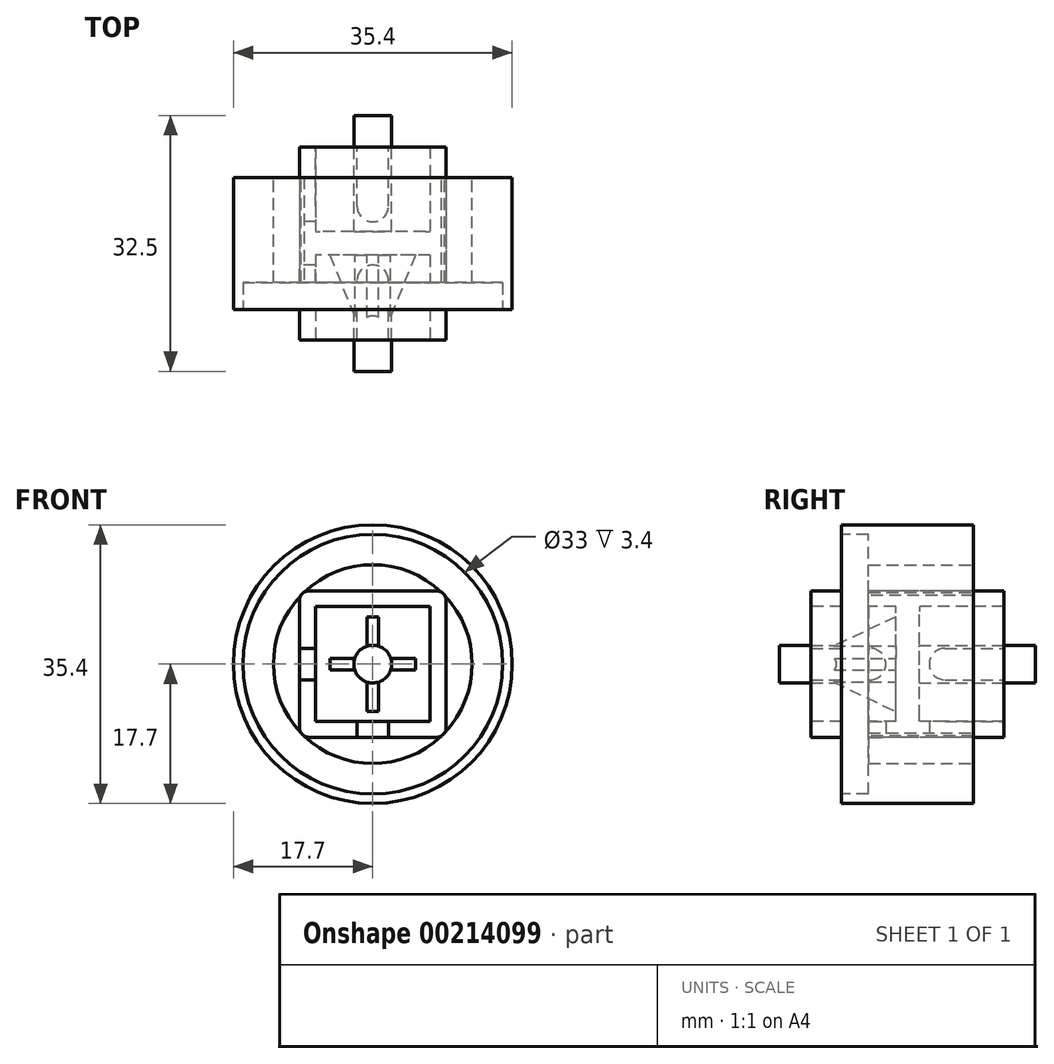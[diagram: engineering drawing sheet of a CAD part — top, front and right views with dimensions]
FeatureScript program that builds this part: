
annotation { "Feature Type Name" : "Feature", "Feature Type Description" : "" }
export const myFeature = defineFeature(function(context is Context, id is Id, definition is map)
    precondition{}
    {
        {
            var Q0;
            Q0=qCreatedBy(makeId("Front.planeOp"),FACE);
            var sketch = newSketch(context, id + "F0", { "sketchPlane" : qUnion([Q0])});
            skCircle(sketch, "E0", {"center": v(0, 0) * mm, "radius": 12.62 * mm});
            skCircle(sketch, "E1", {"center": v(0, 0) * mm, "radius": 17.7 * mm});
            skSolve(sketch);
        }
        {
            var Q0;
            Q0 = qSketchRegion(id + "F0", true);
            extrude(context, id + "F1", {"entities" : qUnion([Q0]), "endBound" : BoundingType.SYMMETRIC, "depth" : 16.75 * mm});
        }
        {
            var Q0;
            Q0=qCreatedBy(makeId("Front.planeOp"),FACE);
            var sketch = newSketch(context, id + "F2", { "sketchPlane" : qUnion([Q0])});
            skLineSegment(sketch, "E2.bottom", {"start": v(-9.3, 9.3) * mm, "end": v(9.3, 9.3) * mm});
            skLineSegment(sketch, "E2.top", {"start": v(-9.3, -9.3) * mm, "end": v(9.3, -9.3) * mm});
            skLineSegment(sketch, "E2.left", {"start": v(-9.3, 9.3) * mm, "end": v(-9.3, -9.3) * mm});
            skLineSegment(sketch, "E2.right", {"start": v(9.3, 9.3) * mm, "end": v(9.3, -9.3) * mm});
            skLineSegment(sketch, "E3", {"start": v(0, 41.14) * mm, "end": v(0, -47.29) * mm, "construction": true});
            skLineSegment(sketch, "E4", {"start": v(-35, 0) * mm, "end": v(39.07, 0) * mm, "construction": true});
            skSolve(sketch);
        }
        {
            var Q0;
            Q0=makeQuery(id+"F2.imprint","IMPRINT",FACE,{"disambiguationData":[TD([[makeQuery(id+"F2.imprint","IMPRINT",EDGE,{"derivedFrom":sQuery(id+"F2.wireOp",EDGE,"E2.bottom")}),-1.0]])]});
            extrude(context, id + "F3", {"entities" : qUnion([Q0]), "endBound" : BoundingType.SYMMETRIC, "oppositeDirection" : true, "depth" : 24.5 * mm});
        }
        {
            var Q0;
            Q0=makeQuery(id+"F3.opExtrude","CAP_FACE",FACE,{"disambiguationData":[OSD([sQuery(id+"F2.wireOp",EDGE,"E2.bottom"),sQuery(id+"F2.wireOp",EDGE,"E2.top"),sQuery(id+"F2.wireOp",EDGE,"E2.left"),sQuery(id+"F2.wireOp",EDGE,"E2.right")])],"isStart":true});
            var sketch = newSketch(context, id + "F4", { "sketchPlane" : qUnion([Q0])});
            skLineSegment(sketch, "E5.bottom", {"start": v(-7.3, 7.3) * mm, "end": v(7.3, 7.3) * mm});
            skLineSegment(sketch, "E5.top", {"start": v(-7.3, -7.3) * mm, "end": v(7.3, -7.3) * mm});
            skLineSegment(sketch, "E5.left", {"start": v(-7.3, 7.3) * mm, "end": v(-7.3, -7.3) * mm});
            skLineSegment(sketch, "E5.right", {"start": v(7.3, 7.3) * mm, "end": v(7.3, -7.3) * mm});
            skSolve(sketch);
        }
        {
            var Q0;
            Q0=makeQuery(id+"F1.opExtrude","CAP_FACE",FACE,{"disambiguationData":[OSD([sQuery(id+"F0.wireOp",EDGE,"E0"),sQuery(id+"F0.wireOp",EDGE,"E1")])],"isStart":false});
            var sketch = newSketch(context, id + "F5", { "sketchPlane" : qUnion([Q0])});
            skCircle(sketch, "E6", {"center": v(0, 0) * mm, "radius": 16.5 * mm});
            skSolve(sketch);
        }
        {
            var Q0;
            Q0 = qSketchRegion(id + "F5", true);
            extrude(context, id + "F6", {"entities" : qUnion([Q0]), "operationType" : NewBodyOperationType.REMOVE, "oppositeDirection" : true, "depth" : 3.4 * mm});
        }
        {
            var Q0;
            Q0=makeQuery(id+"F3.opExtrude","SWEPT_EDGE",EDGE,{"disambiguationData":[OSD([sQuery(id+"F2.wireOp",EDGE,"E2.bottom"),sQuery(id+"F2.wireOp",EDGE,"E2.left")])]});
            var Q1;
            Q1=makeQuery(id+"F3.opExtrude","SWEPT_EDGE",EDGE,{"disambiguationData":[OSD([sQuery(id+"F2.wireOp",EDGE,"E2.top"),sQuery(id+"F2.wireOp",EDGE,"E2.left")])]});
            var Q2;
            Q2=makeQuery(id+"F3.opExtrude","SWEPT_EDGE",EDGE,{"disambiguationData":[OSD([sQuery(id+"F2.wireOp",EDGE,"E2.top"),sQuery(id+"F2.wireOp",EDGE,"E2.right")])]});
            var Q3;
            Q3=makeQuery(id+"F3.opExtrude","SWEPT_EDGE",EDGE,{"disambiguationData":[OSD([sQuery(id+"F2.wireOp",EDGE,"E2.bottom"),sQuery(id+"F2.wireOp",EDGE,"E2.right")])]});
            fillet(context, id + "F7", {"entities" : qUnion([Q0, Q1, Q2, Q3]), "radius" : 1.2 * mm, "tangentPropagation" : true, "allowEdgeOverflow" : false});
        }
        {
            var Q0;
            Q0 = qSketchRegion(id + "F4", true);
            extrude(context, id + "F8", {"entities" : qUnion([Q0]), "operationType" : NewBodyOperationType.REMOVE, "endBound" : BoundingType.THROUGH_ALL, "oppositeDirection" : true, "depth" : 10 * mm});
        }
        {
            var Q0;
            Q0=qCreatedBy(makeId("Front.planeOp"),FACE);
            var sketch = newSketch(context, id + "F9", { "sketchPlane" : qUnion([Q0])});
            skLineSegment(sketch, "E7.0", {"start": v(-9.3, 8.1) * mm, "end": v(-9.3, -8.1) * mm});
            skLineSegment(sketch, "E7.1", {"start": v(-8.1, 9.3) * mm, "end": v(8.1, 9.3) * mm});
            skArc(sketch, "E7.2", {"start": v(-8.1, 9.3) * mm, "mid": v(-8.95, 8.95) * mm, "end": v(-9.3, 8.1) * mm});
            skArc(sketch, "E7.3", {"start": v(9.3, 8.1) * mm, "mid": v(8.95, 8.95) * mm, "end": v(8.1, 9.3) * mm});
            skLineSegment(sketch, "E7.4", {"start": v(9.3, 8.1) * mm, "end": v(9.3, -8.1) * mm});
            skArc(sketch, "E7.5", {"start": v(-9.3, -8.1) * mm, "mid": v(-8.95, -8.95) * mm, "end": v(-8.1, -9.3) * mm});
            skLineSegment(sketch, "E7.6", {"start": v(-8.1, -9.3) * mm, "end": v(8.1, -9.3) * mm});
            skArc(sketch, "E7.7", {"start": v(8.1, -9.3) * mm, "mid": v(8.95, -8.95) * mm, "end": v(9.3, -8.1) * mm});
            skSolve(sketch);
        }
        {
            var Q0;
            Q0 = qSketchRegion(id + "F9", true);
            extrude(context, id + "F10", {"entities" : qUnion([Q0]), "operationType" : NewBodyOperationType.ADD, "endBound" : BoundingType.SYMMETRIC, "depth" : 3 * mm});
        }
        {
            var Q0;
            Q0=qCreatedBy(makeId("Front.planeOp"),FACE);
            var sketch = newSketch(context, id + "F11", { "sketchPlane" : qUnion([Q0])});
            skCircle(sketch, "E8", {"center": v(0, 0) * mm, "radius": 2.4 * mm});
            skSolve(sketch);
        }
        {
            var Q0;
            Q0 = qSketchRegion(id + "F11", true);
            extrude(context, id + "F12", {"entities" : qUnion([Q0]), "operationType" : NewBodyOperationType.ADD, "endBound" : BoundingType.SYMMETRIC, "depth" : 32.5 * mm});
        }
        {
            var Q0;
            {var subQ0=sQuery(id+"F4.wireOp",EDGE,"E5.top");var subQ1=sQuery(id+"F4.wireOp",EDGE,"E5.left");Q0=makeQuery(id+"F10.boolean.opBoolean","SPLIT",EDGE,{"disambiguationData":[TD([makeQuery(id+"F3.opExtrude","CAP_FACE",FACE,{"disambiguationData":[OSD([sQuery(id+"F2.wireOp",EDGE,"E2.bottom"),sQuery(id+"F2.wireOp",EDGE,"E2.top"),sQuery(id+"F2.wireOp",EDGE,"E2.left"),sQuery(id+"F2.wireOp",EDGE,"E2.right")])],"isStart":false})])],"derivedFrom":makeQuery(id+"F8.boolean.opBoolean","COPY",EDGE,{"derivedFrom":makeQuery(id+"F8.opExtrude","SWEPT_EDGE",EDGE,{"disambiguationData":[OSD([subQ0,subQ1])]})})});}
            var Q1;
            {var subQ0=sQuery(id+"F4.wireOp",EDGE,"E5.bottom");var subQ1=sQuery(id+"F4.wireOp",EDGE,"E5.left");Q1=makeQuery(id+"F10.boolean.opBoolean","SPLIT",EDGE,{"disambiguationData":[TD([makeQuery(id+"F3.opExtrude","CAP_FACE",FACE,{"disambiguationData":[OSD([sQuery(id+"F2.wireOp",EDGE,"E2.bottom"),sQuery(id+"F2.wireOp",EDGE,"E2.top"),sQuery(id+"F2.wireOp",EDGE,"E2.left"),sQuery(id+"F2.wireOp",EDGE,"E2.right")])],"isStart":false})])],"derivedFrom":makeQuery(id+"F8.boolean.opBoolean","COPY",EDGE,{"derivedFrom":makeQuery(id+"F8.opExtrude","SWEPT_EDGE",EDGE,{"disambiguationData":[OSD([subQ0,subQ1])]})})});}
            var Q2;
            {var subQ0=sQuery(id+"F4.wireOp",EDGE,"E5.bottom");var subQ1=sQuery(id+"F4.wireOp",EDGE,"E5.right");Q2=makeQuery(id+"F10.boolean.opBoolean","SPLIT",EDGE,{"disambiguationData":[TD([makeQuery(id+"F3.opExtrude","CAP_FACE",FACE,{"disambiguationData":[OSD([sQuery(id+"F2.wireOp",EDGE,"E2.bottom"),sQuery(id+"F2.wireOp",EDGE,"E2.top"),sQuery(id+"F2.wireOp",EDGE,"E2.left"),sQuery(id+"F2.wireOp",EDGE,"E2.right")])],"isStart":false})])],"derivedFrom":makeQuery(id+"F8.boolean.opBoolean","COPY",EDGE,{"derivedFrom":makeQuery(id+"F8.opExtrude","SWEPT_EDGE",EDGE,{"disambiguationData":[OSD([subQ0,subQ1])]})})});}
            var Q3;
            {var subQ0=sQuery(id+"F4.wireOp",EDGE,"E5.top");var subQ1=sQuery(id+"F4.wireOp",EDGE,"E5.right");Q3=makeQuery(id+"F10.boolean.opBoolean","SPLIT",EDGE,{"disambiguationData":[TD([makeQuery(id+"F3.opExtrude","CAP_FACE",FACE,{"disambiguationData":[OSD([sQuery(id+"F2.wireOp",EDGE,"E2.bottom"),sQuery(id+"F2.wireOp",EDGE,"E2.top"),sQuery(id+"F2.wireOp",EDGE,"E2.left"),sQuery(id+"F2.wireOp",EDGE,"E2.right")])],"isStart":false})])],"derivedFrom":makeQuery(id+"F8.boolean.opBoolean","COPY",EDGE,{"derivedFrom":makeQuery(id+"F8.opExtrude","SWEPT_EDGE",EDGE,{"disambiguationData":[OSD([subQ0,subQ1])]})})});}
            var Q4;
            {var subQ0=sQuery(id+"F4.wireOp",EDGE,"E5.top");var subQ1=sQuery(id+"F4.wireOp",EDGE,"E5.right");Q4=makeQuery(id+"F10.boolean.opBoolean","SPLIT",EDGE,{"disambiguationData":[TD([makeQuery(id+"F3.opExtrude","CAP_FACE",FACE,{"disambiguationData":[OSD([sQuery(id+"F2.wireOp",EDGE,"E2.bottom"),sQuery(id+"F2.wireOp",EDGE,"E2.top"),sQuery(id+"F2.wireOp",EDGE,"E2.left"),sQuery(id+"F2.wireOp",EDGE,"E2.right")])],"isStart":true})])],"derivedFrom":makeQuery(id+"F8.boolean.opBoolean","COPY",EDGE,{"derivedFrom":makeQuery(id+"F8.opExtrude","SWEPT_EDGE",EDGE,{"disambiguationData":[OSD([subQ0,subQ1])]})})});}
            var Q5;
            {var subQ0=sQuery(id+"F4.wireOp",EDGE,"E5.top");var subQ1=sQuery(id+"F4.wireOp",EDGE,"E5.left");Q5=makeQuery(id+"F10.boolean.opBoolean","SPLIT",EDGE,{"disambiguationData":[TD([makeQuery(id+"F3.opExtrude","CAP_FACE",FACE,{"disambiguationData":[OSD([sQuery(id+"F2.wireOp",EDGE,"E2.bottom"),sQuery(id+"F2.wireOp",EDGE,"E2.top"),sQuery(id+"F2.wireOp",EDGE,"E2.left"),sQuery(id+"F2.wireOp",EDGE,"E2.right")])],"isStart":true})])],"derivedFrom":makeQuery(id+"F8.boolean.opBoolean","COPY",EDGE,{"derivedFrom":makeQuery(id+"F8.opExtrude","SWEPT_EDGE",EDGE,{"disambiguationData":[OSD([subQ0,subQ1])]})})});}
            var Q6;
            {var subQ0=sQuery(id+"F4.wireOp",EDGE,"E5.bottom");var subQ1=sQuery(id+"F4.wireOp",EDGE,"E5.right");Q6=makeQuery(id+"F10.boolean.opBoolean","SPLIT",EDGE,{"disambiguationData":[TD([makeQuery(id+"F3.opExtrude","CAP_FACE",FACE,{"disambiguationData":[OSD([sQuery(id+"F2.wireOp",EDGE,"E2.bottom"),sQuery(id+"F2.wireOp",EDGE,"E2.top"),sQuery(id+"F2.wireOp",EDGE,"E2.left"),sQuery(id+"F2.wireOp",EDGE,"E2.right")])],"isStart":true})])],"derivedFrom":makeQuery(id+"F8.boolean.opBoolean","COPY",EDGE,{"derivedFrom":makeQuery(id+"F8.opExtrude","SWEPT_EDGE",EDGE,{"disambiguationData":[OSD([subQ0,subQ1])]})})});}
            var Q7;
            {var subQ0=sQuery(id+"F4.wireOp",EDGE,"E5.bottom");var subQ1=sQuery(id+"F4.wireOp",EDGE,"E5.left");Q7=makeQuery(id+"F10.boolean.opBoolean","SPLIT",EDGE,{"disambiguationData":[TD([makeQuery(id+"F3.opExtrude","CAP_FACE",FACE,{"disambiguationData":[OSD([sQuery(id+"F2.wireOp",EDGE,"E2.bottom"),sQuery(id+"F2.wireOp",EDGE,"E2.top"),sQuery(id+"F2.wireOp",EDGE,"E2.left"),sQuery(id+"F2.wireOp",EDGE,"E2.right")])],"isStart":true})])],"derivedFrom":makeQuery(id+"F8.boolean.opBoolean","COPY",EDGE,{"derivedFrom":makeQuery(id+"F8.opExtrude","SWEPT_EDGE",EDGE,{"disambiguationData":[OSD([subQ0,subQ1])]})})});}
            fillet(context, id + "F13", {"entities" : qUnion([Q0, Q1, Q2, Q3, Q4, Q5, Q6, Q7]), "radius" : 0.6 * mm, "tangentPropagation" : true, "allowEdgeOverflow" : false});
        }
        {
            var Q0;
            Q0=qCreatedBy(makeId("Right.planeOp"),FACE);
            var sketch = newSketch(context, id + "F14", { "sketchPlane" : qUnion([Q0])});
            skLineSegment(sketch, "E9", {"start": v(-23.25, 0) * mm, "end": v(19.17, 0) * mm, "construction": true});
            skLineSegment(sketch, "E10", {"start": v(-10, 2) * mm, "end": v(-10, -2) * mm});
            skLineSegment(sketch, "E11", {"start": v(-10, -2) * mm, "end": v(-1.5, -6) * mm});
            skLineSegment(sketch, "E12", {"start": v(-1.5, -6) * mm, "end": v(-1.5, 6) * mm});
            skLineSegment(sketch, "E13", {"start": v(-1.5, 6) * mm, "end": v(-10, 2) * mm});
            skSolve(sketch);
        }
        {
            var Q0;
            Q0=makeQuery(id+"F3.opExtrude","SWEPT_FACE",FACE,{"disambiguationData":[OSD([sQuery(id+"F2.wireOp",EDGE,"E2.top")])]});
            var sketch = newSketch(context, id + "F15", { "sketchPlane" : qUnion([Q0])});
            skLineSegment(sketch, "E14", {"start": v(0, 20.63) * mm, "end": v(0, -24.57) * mm, "construction": true});
            skPoint(sketch, "E14.endSnap0", {"position": v(0, -12.25) * mm});
            skLineSegment(sketch, "E15.bottom", {"start": v(-2, 12.25) * mm, "end": v(2, 12.25) * mm});
            skLineSegment(sketch, "E15.left", {"start": v(-2, 12.25) * mm, "end": v(-2, 4.75) * mm});
            skLineSegment(sketch, "E15.right", {"start": v(2, 12.25) * mm, "end": v(2, 4.75) * mm});
            skArc(sketch, "E16", {"start": v(-2, 4.75) * mm, "mid": v(0, 2.75) * mm, "end": v(2, 4.75) * mm});
            skLineSegment(sketch, "E17.MirrorCS", {"start": v(2, -12.25) * mm, "end": v(2, -4.75) * mm});
            skLineSegment(sketch, "E18.MirrorCS", {"start": v(-2, -12.25) * mm, "end": v(2, -12.25) * mm});
            skLineSegment(sketch, "E19.MirrorCS", {"start": v(-2, -12.25) * mm, "end": v(-2, -4.75) * mm});
            skArc(sketch, "E20.MirrorCS", {"start": v(-2, -4.75) * mm, "mid": v(0, -2.75) * mm, "end": v(2, -4.75) * mm});
            skSolve(sketch);
        }
        {
            var Q0;
            Q0 = qSketchRegion(id + "F15", true);
            extrude(context, id + "F16", {"entities" : qUnion([Q0]), "operationType" : NewBodyOperationType.REMOVE, "endBound" : BoundingType.UP_TO_NEXT, "oppositeDirection" : true, "depth" : 25 * mm});
        }
        {
            var Q0;
            Q0=makeQuery(id+"F3.opExtrude","SWEPT_FACE",FACE,{"disambiguationData":[OSD([sQuery(id+"F2.wireOp",EDGE,"E2.left")])]});
            var sketch = newSketch(context, id + "F17", { "sketchPlane" : qUnion([Q0])});
            skLineSegment(sketch, "E21.bottom", {"start": v(12.25, 2) * mm, "end": v(4.75, 2) * mm});
            skLineSegment(sketch, "E21.top", {"start": v(12.25, -2) * mm, "end": v(4.75, -2) * mm});
            skLineSegment(sketch, "E21.left", {"start": v(12.25, 2) * mm, "end": v(12.25, -2) * mm});
            skArc(sketch, "E22", {"start": v(4.75, 2) * mm, "mid": v(2.75, 0) * mm, "end": v(4.75, -2) * mm});
            skArc(sketch, "E23.MirrorCS", {"start": v(-4.75, 2) * mm, "mid": v(-2.75, 0) * mm, "end": v(-4.75, -2) * mm});
            skLineSegment(sketch, "E24.MirrorCS", {"start": v(-12.25, -2) * mm, "end": v(-4.75, -2) * mm});
            skLineSegment(sketch, "E25.MirrorCS", {"start": v(-12.25, 2) * mm, "end": v(-4.75, 2) * mm});
            skLineSegment(sketch, "E26.MirrorCS", {"start": v(-12.25, 2) * mm, "end": v(-12.25, -2) * mm});
            skSolve(sketch);
        }
        {
            var Q0;
            Q0 = qSketchRegion(id + "F17", true);
            extrude(context, id + "F18", {"entities" : qUnion([Q0]), "operationType" : NewBodyOperationType.REMOVE, "endBound" : BoundingType.UP_TO_NEXT, "oppositeDirection" : true, "depth" : 25 * mm});
        }
        {
            var Q0;
            Q0 = qSketchRegion(id + "F14", true);
            extrude(context, id + "F19", {"entities" : qUnion([Q0]), "operationType" : NewBodyOperationType.ADD, "endBound" : BoundingType.SYMMETRIC, "depth" : 1.5 * mm});
        }
        {
            var Q0;
            Q0=qCreatedBy(makeId("Top.planeOp"),FACE);
            var sketch = newSketch(context, id + "F20", { "sketchPlane" : qUnion([Q0])});
            skLineSegment(sketch, "E27", {"start": v(0, -29.25) * mm, "end": v(0, 24.16) * mm, "construction": true});
            skLineSegment(sketch, "E28", {"start": v(2, -10) * mm, "end": v(-2, -10) * mm});
            skLineSegment(sketch, "E29", {"start": v(-2, -10) * mm, "end": v(-6, 0) * mm});
            skLineSegment(sketch, "E30", {"start": v(-6, 0) * mm, "end": v(6, 0) * mm});
            skLineSegment(sketch, "E31", {"start": v(6, 0) * mm, "end": v(2, -10) * mm});
            skSolve(sketch);
        }
        {
            var Q0;
            Q0 = qSketchRegion(id + "F20", true);
            extrude(context, id + "F21", {"entities" : qUnion([Q0]), "operationType" : NewBodyOperationType.ADD, "endBound" : BoundingType.SYMMETRIC, "depth" : 1.5 * mm});
        }
    });
